# Revit family: CF4K-00X9AZOU05
name_source: partatom
category: Luminarias
units: mm (PartAtom-declared; Revit-internal decimal feet)

## family parameters
Anfitrión = Cara
Compartido = Sí
Corte con vacíos al cargar = No
Cota de conector redondo = Diámetro de uso
Número OmniClass = 23.80.70.00
Origen de luz = No
Punto de cálculo de habitación = No
Tipo de pieza = Normal
Título OmniClass = Lighting

## types (1)
- CF4K-00X9AZOU05
    Acabado = Black, Opal
    CRI = 90
    Carga aparente = 0 VA
    Catálogo = Decorative
    CodigoGubimclass = 50.60.50.20
    CodigoOmniclass = 21-04 50 40
    CodigoUniclass2015 = EF_70_80
    CodigoUniformat2010 = D5040
    DescripcionGubimclass = Iluminación interior
    DescripcionOmniclass = Lighting
    DescripcionUniclass2015 = Lighting
    DescripcionUniformat2010 = Lighting
    EAN13 = 8435575379770
    Eficiencia energética = E
    Elevación por defecto = 1000 mm  [stored 3.28084 ft]
    Etiqueta V/f = 100-240V/50-60Hz
    Fabricante = LEDS C4
    Familia = Circular Outward ø900 Surface
    FechaVersion = Creada: 31/03/2023
    Ficha = https://files.ledsc4.com
    Fotometría = https://files.ledsc4.com
    IMC = https://files.ledsc4.com
    IP = IP20
    IfcExportAs = IfcLightFixture
IfcLightFixture
    IfcExportType = NOTDEFINED
    Imagen web = https://files.ledsc4.com
    LDT = https://files.ledsc4.com
    Lumenes reales (lm) = 4159
    Material = Aluminium, Polycarbonate
    Peso neto (KG) = 5
    Producto descatalogado = Catalogado EN
    Referencia = CF4K-00X9AZOU05
    Temperatura color led (K) = LED neutral-white 4000K
    Tender text (Castellano) = LedsC4 Circular Outward ø900 Surface CF4K-00X9AZOU05V1  Pendant for indoor use.  Structure material: Aluminium. Structure finish: Black. Diffuser material: Polycarbonate. Diffuser finish: Opal. Warranty: 5 Years.  Product net weight (Kg): 5 Product width or diameter (mm): 884 Product height (mm): 300  Class 1. IP: IP20. LED. No. of lampholders or LEDs: 1. Driver brand: MEANWELL. Maximum power of light source: 49.6W. Colour temperature: 4000K. Colour rendering index: 90. Hours of life: 50.000h L80B20. UGR: 9.3. Real flux (lm): 4159. Real lm/W: 78. Voltage / frequency range: 90-305/50-60Hz. Voltage: 2,8. Equipment included: Yes. Total power: 53. Power factor: 0.90. Dimmable equipment included: ON-OFF.
    Tender text (English) = LedsC4 Circular Outward ø900 Surface CF4K-00X9AZOU05V1  Pendant for indoor use.  Structure material: Aluminium. Structure finish: Black. Diffuser material: Polycarbonate. Diffuser finish: Opal. Warranty: 5 Years.  Product net weight (Kg): 5 Product width or diameter (mm): 884 Product height (mm): 300  Class 1. IP: IP20. LED. No. of lampholders or LEDs: 1. Driver brand: MEANWELL. Maximum power of light source: 49.6W. Colour temperature: 4000K. Colour rendering index: 90. Hours of life: 50.000h L80B20. UGR: 9.3. Real flux (lm): 4159. Real lm/W: 78. Voltage / frequency range: 90-305/50-60Hz. Voltage: 2,8. Equipment included: Yes. Total power: 53. Power factor: 0.90. Dimmable equipment included: ON-OFF.
    Tipo = Pendant
    Tipo de regulación = ON-OFF
    Vatios (W) = 53
    Versión = v1

note: [stored X ft] marks values corroborated as IEEE doubles in the binary element streams (Revit-internal decimal feet)
